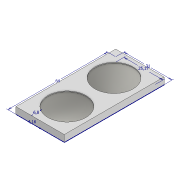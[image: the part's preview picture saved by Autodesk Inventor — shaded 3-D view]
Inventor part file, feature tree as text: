
AUTODESK INVENTOR PART (.ipt)
format: ipt  version: 2020.3 (Build 243373000, 373)  size: 111,616 bytes
history: native  units: mm
features: extrude x3, sketch x2
ambient origin geometry x8: Origin, YZ Plane, XZ Plane, XY Plane, X Axis, Y Axis, Z Axis, Center Point
bodies: Solid1 (feature_tree)
feature tree (5):
  sketch  "Sketch1"  dims[d0=31.0mm d1=64.0mm]
  extrude  "Extrusion1"  Depth=64.0mm
  extrude  "Extrusion2"  Depth=0.5mm
  extrude  "Extrusion3"  Depth=0.5mm
  sketch  "Sketch2"  dims[d2=25.17mm d4=4.16mm d5=6.8mm d6=4.3mm d7=0.0mm d8=1.75mm d9=0.0mm d10=24.5mm d11=4.34mm d13=28.66mm d14=0.5mm d15=0.0mm]
